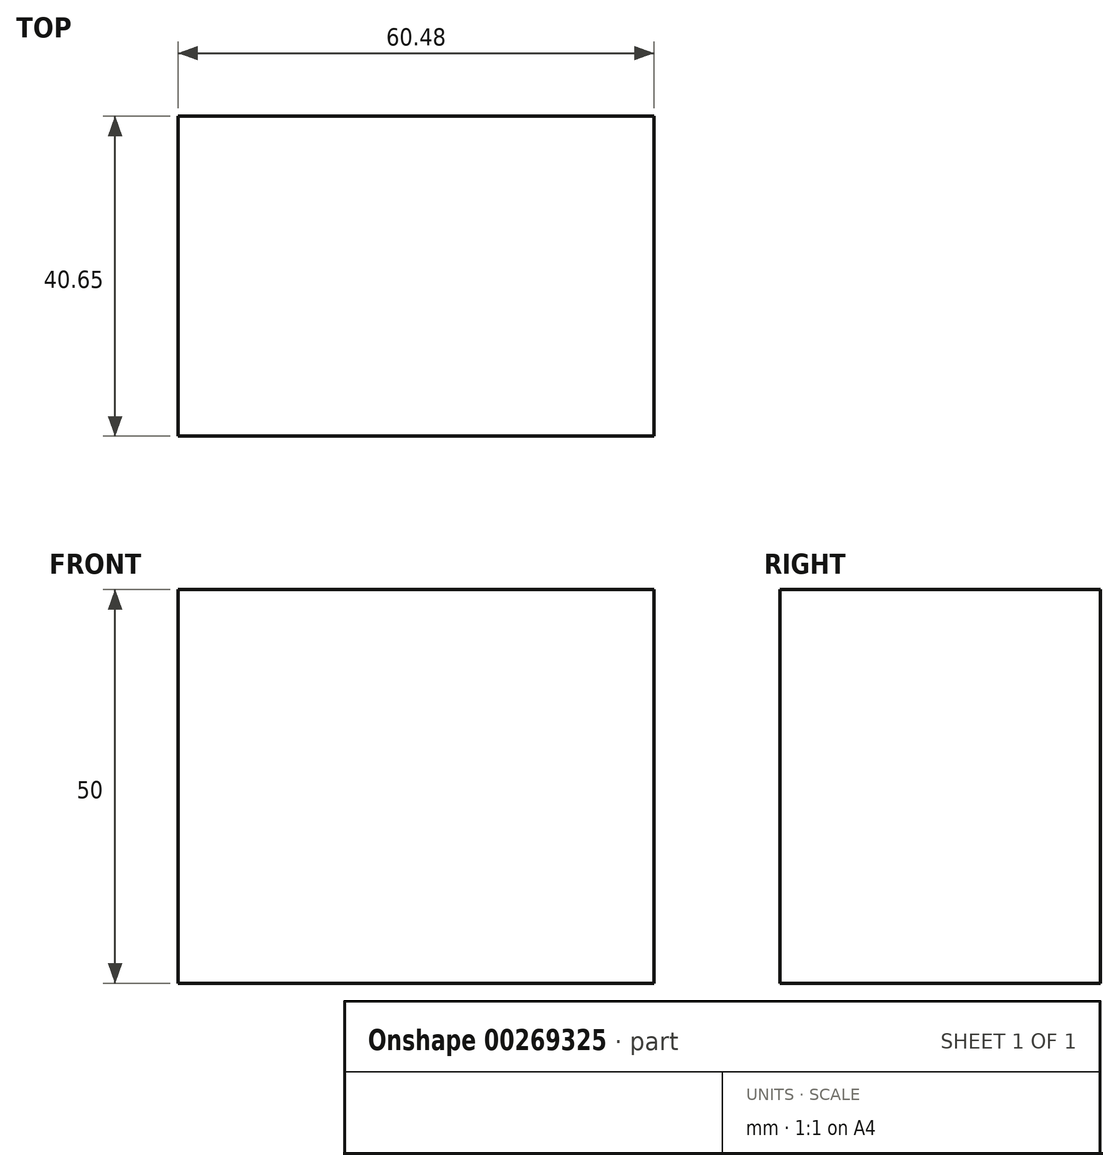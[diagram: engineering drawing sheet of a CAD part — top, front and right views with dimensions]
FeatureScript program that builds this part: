
annotation { "Feature Type Name" : "Feature", "Feature Type Description" : "" }
export const myFeature = defineFeature(function(context is Context, id is Id, definition is map)
    precondition{}
    {
        {
            var Q0;
            Q0=qCreatedBy(makeId("Top.planeOp"),FACE);
            var sketch = newSketch(context, id + "F0", { "sketchPlane" : qUnion([Q0])});
            skLineSegment(sketch, "E0.bottom", {"start": v(-51.57, -35.5) * mm, "end": v(8.9, -35.5) * mm});
            skLineSegment(sketch, "E0.top", {"start": v(-51.57, 5.14) * mm, "end": v(8.9, 5.14) * mm});
            skLineSegment(sketch, "E0.left", {"start": v(-51.57, -35.5) * mm, "end": v(-51.57, 5.14) * mm});
            skLineSegment(sketch, "E0.right", {"start": v(8.9, -35.5) * mm, "end": v(8.9, 5.14) * mm});
            skSolve(sketch);
        }
        {
            var Q0;
            Q0 = qSketchRegion(id + "F0", true);
            extrude(context, id + "F1", {"entities" : qUnion([Q0]), "depth" : 50 * mm, "offsetDistance" : 25 * mm});
        }
    });
